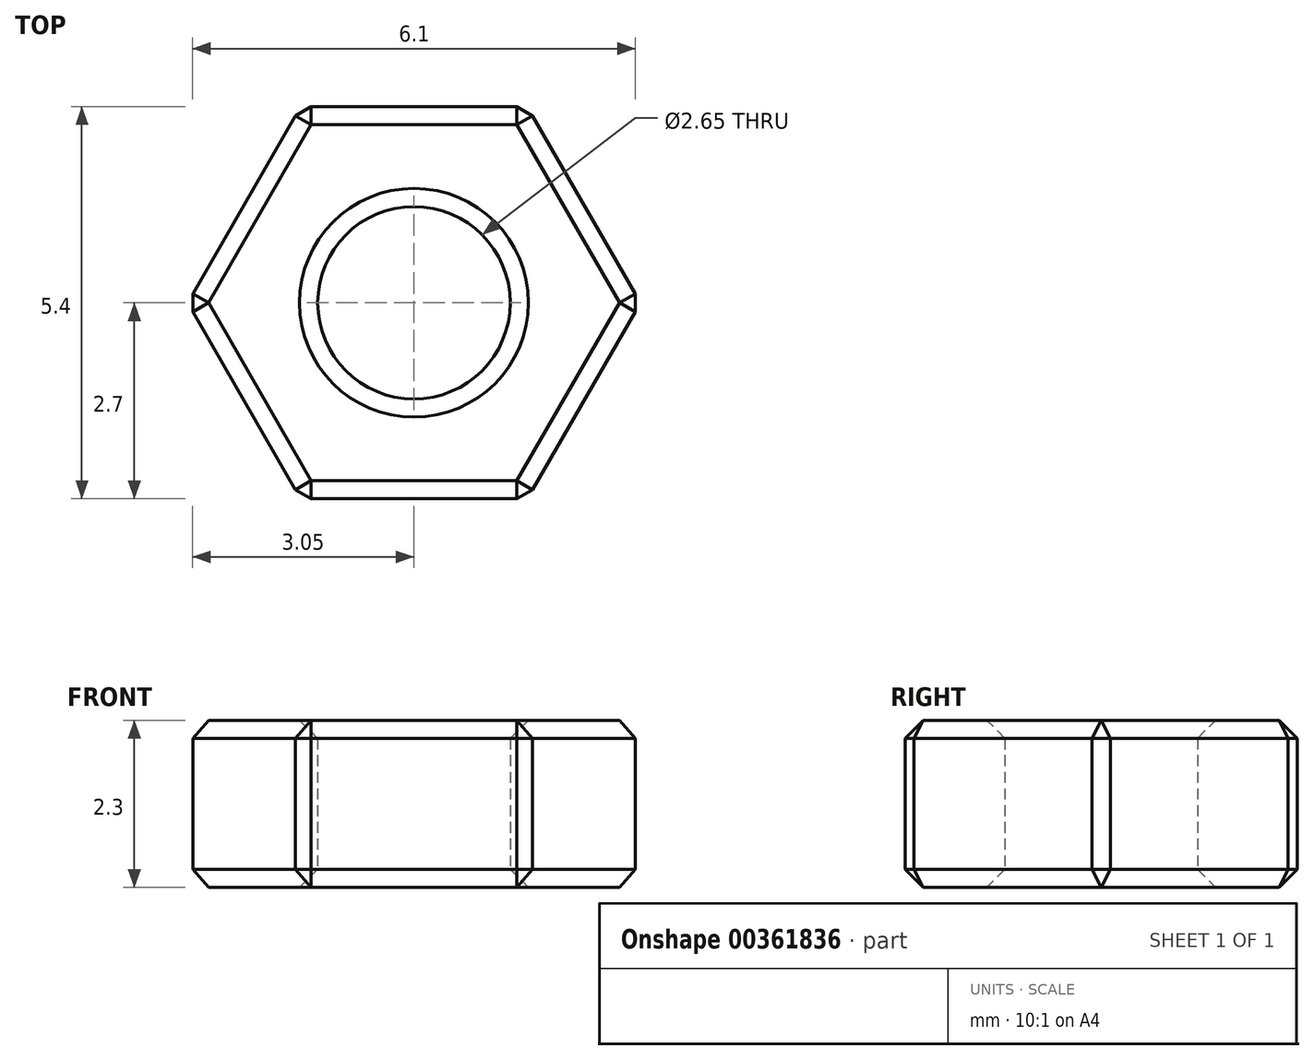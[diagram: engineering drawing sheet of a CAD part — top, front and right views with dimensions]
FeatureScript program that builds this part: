
annotation { "Feature Type Name" : "Feature", "Feature Type Description" : "" }
export const myFeature = defineFeature(function(context is Context, id is Id, definition is map)
    precondition{}
    {
        {
            var Q0;
            Q0=qCreatedBy(makeId("Top.planeOp"),FACE);
            var sketch = newSketch(context, id + "F0", { "sketchPlane" : qUnion([Q0])});
            skCircle(sketch, "E0.cCircle", {"center": v(0, 0) * mm, "radius": 2.7 * mm, "construction": true});
            skLineSegment(sketch, "E0.0", {"start": v(-3.12, 0) * mm, "end": v(-1.56, 2.7) * mm});
            skLineSegment(sketch, "E0.1", {"start": v(-1.56, 2.7) * mm, "end": v(1.56, 2.7) * mm});
            skLineSegment(sketch, "E0.2", {"start": v(1.56, 2.7) * mm, "end": v(3.12, 0) * mm});
            skLineSegment(sketch, "E0.3", {"start": v(3.12, 0) * mm, "end": v(1.56, -2.7) * mm});
            skLineSegment(sketch, "E0.4", {"start": v(1.56, -2.7) * mm, "end": v(-1.56, -2.7) * mm});
            skLineSegment(sketch, "E0.5", {"start": v(-1.56, -2.7) * mm, "end": v(-3.12, 0) * mm});
            skPoint(sketch, "E0.0.midPoint", {"position": v(-2.34, 1.35) * mm});
            skCircle(sketch, "E1", {"center": v(0, 0) * mm, "radius": 1.32 * mm});
            skSolve(sketch);
        }
        {
            var Q0;
            Q0=makeQuery(id+"F0.imprint","IMPRINT",FACE,{"disambiguationData":[TD([[makeQuery(id+"F0.imprint","IMPRINT",EDGE,{"derivedFrom":sQuery(id+"F0.wireOp",EDGE,"E0.0")}),-1.0]])]});
            extrude(context, id + "F1", {"entities" : qUnion([Q0]), "depth" : 2.3 * mm, "offsetDistance" : 25 * mm});
        }
        {
            var Q0;
            Q0=makeQuery(id+"F1.opExtrude","CAP_EDGE",EDGE,{"disambiguationData":[OSD([sQuery(id+"F0.wireOp",EDGE,"E1")])],"isStart":false});
            var Q1;
            Q1=makeQuery(id+"F1.opExtrude","CAP_EDGE",EDGE,{"disambiguationData":[OSD([sQuery(id+"F0.wireOp",EDGE,"E1")])],"isStart":true});
            var Q2;
            Q2=makeQuery(id+"F1.opExtrude","CAP_EDGE",EDGE,{"disambiguationData":[OSD([sQuery(id+"F0.wireOp",EDGE,"E0.5")])],"isStart":true});
            var Q3;
            Q3=makeQuery(id+"F1.opExtrude","CAP_EDGE",EDGE,{"disambiguationData":[OSD([sQuery(id+"F0.wireOp",EDGE,"E0.4")])],"isStart":true});
            var Q4;
            Q4=makeQuery(id+"F1.opExtrude","CAP_EDGE",EDGE,{"disambiguationData":[OSD([sQuery(id+"F0.wireOp",EDGE,"E0.3")])],"isStart":true});
            var Q5;
            Q5=makeQuery(id+"F1.opExtrude","CAP_EDGE",EDGE,{"disambiguationData":[OSD([sQuery(id+"F0.wireOp",EDGE,"E0.2")])],"isStart":true});
            var Q6;
            Q6=makeQuery(id+"F1.opExtrude","CAP_EDGE",EDGE,{"disambiguationData":[OSD([sQuery(id+"F0.wireOp",EDGE,"E0.1")])],"isStart":true});
            var Q7;
            Q7=makeQuery(id+"F1.opExtrude","CAP_EDGE",EDGE,{"disambiguationData":[OSD([sQuery(id+"F0.wireOp",EDGE,"E0.0")])],"isStart":true});
            var Q8;
            Q8=makeQuery(id+"F1.opExtrude","SWEPT_FACE",FACE,{"disambiguationData":[OSD([sQuery(id+"F0.wireOp",EDGE,"E0.4")])]});
            var Q9;
            Q9=makeQuery(id+"F1.opExtrude","SWEPT_FACE",FACE,{"disambiguationData":[OSD([sQuery(id+"F0.wireOp",EDGE,"E0.5")])]});
            var Q10;
            Q10=makeQuery(id+"F1.opExtrude","SWEPT_FACE",FACE,{"disambiguationData":[OSD([sQuery(id+"F0.wireOp",EDGE,"E0.3")])]});
            var Q11;
            Q11=makeQuery(id+"F1.opExtrude","SWEPT_FACE",FACE,{"disambiguationData":[OSD([sQuery(id+"F0.wireOp",EDGE,"E0.2")])]});
            var Q12;
            Q12=makeQuery(id+"F1.opExtrude","SWEPT_FACE",FACE,{"disambiguationData":[OSD([sQuery(id+"F0.wireOp",EDGE,"E0.1")])]});
            var Q13;
            Q13=makeQuery(id+"F1.opExtrude","SWEPT_FACE",FACE,{"disambiguationData":[OSD([sQuery(id+"F0.wireOp",EDGE,"E0.0")])]});
            chamfer(context, id + "F2", {"entities" : qUnion([Q0, Q1, Q2, Q3, Q4, Q5, Q6, Q7, Q8, Q9, Q10, Q11, Q12, Q13]), "width" : .25 * mm, "tangentPropagation" : true});
        }
    });
